# Revit family: ДСП-01 60 Вт 1500
name_source: partatom
category: Осветительные приборы
units: mm (PartAtom-declared; Revit-internal decimal feet)

## family parameters
Всегда вертикально = Да
Заголовок OmniClass = Luminaries for Internal Lighting
Источник света = Да
Номер OmniClass = 23.80.70.11
Общий = Нет
Основа = Потолок
При загрузке вырезать с полостями = Нет
Размер круглого соединителя = Использовать диаметр
Тип детали = Нормальный
Точка расчета площади = Нет

## types (2) — shared parameters
ADSK_Размер_Высота = 75 мм
ADSK_Размер_Длина = 1490 мм
ADSK_Размер_Ширина = 95 мм
URL = http://innolux.pro
Блок аварийного питания = нет
Бренд светодиодов = EDISON
Вес светильника = 1.7 кг
Время импульса пускового тока = 26 мс
Гарантия = 7 лет
Диапазон рабочих температур = - 40 + 40°C
Диммирование = нет
Изготовитель = INNOLUX
Индекс цветопередачи = >80
Категория по ограничению яркости = 1
Класс защиты от поражения током = I
Класс светораспределения по ГОСТ 54350-2011 = П
Климатическое исполнение = УХЛ 1
Кол-во светодиодов = 150
Количество в упаковке = 1
Количество модулей = 1
Коэффициент мощности = >0.95
>0.95
>0.95
Коэффициент пульсации = <5%
Материал клипс = Алюминий
Материал корпуса = Поликарбонат, прозрачный(1)
Материал рассеивателя = Поликарбонат, прозрачный
Напряжение = 176-264 В
Объём упаковки = 1500х110х85 мм
Полная установленная мощность = 60 В·А
Потребляемый ток = 0
Пусковой ток = 17 А
Световой поток модуля = 8000
Светофильтр = 16777215
Сила тока = 0.27 А
Смещение цветовой температуры при затухании лампы = <Нет>
Способ монтажа = накладной / подвесной
Срок службы = 80000
Степень защиты (IP) = IP65
Тип кривой силы света по ГОСТ 54350-2011 = Д
Тип рассеивателя = призматический опал
Типоразмер светодиода = 2835
Угол наклона = 90.00°
Ударопрочность = IK08
Цвет корпуса = Серый
Частота сети = 50 / 60 Гц
Эффективность светильника = 118

## per-type parameters (varying)
| type | Артикул | Файл фотометрической сетки |
| ДСП-01-ПП-60-1500-4К-IP65 | 14 733 | INNOLUX 14 733 DSP-01-PP-60-1500-4K-IP65.ies |
| ДСП-01-ПП-60-1500-5К-IP65 | 14 734 | INNOLUX 14 734 DSP-01-PP-60-1500-5K-IP65.ies |
